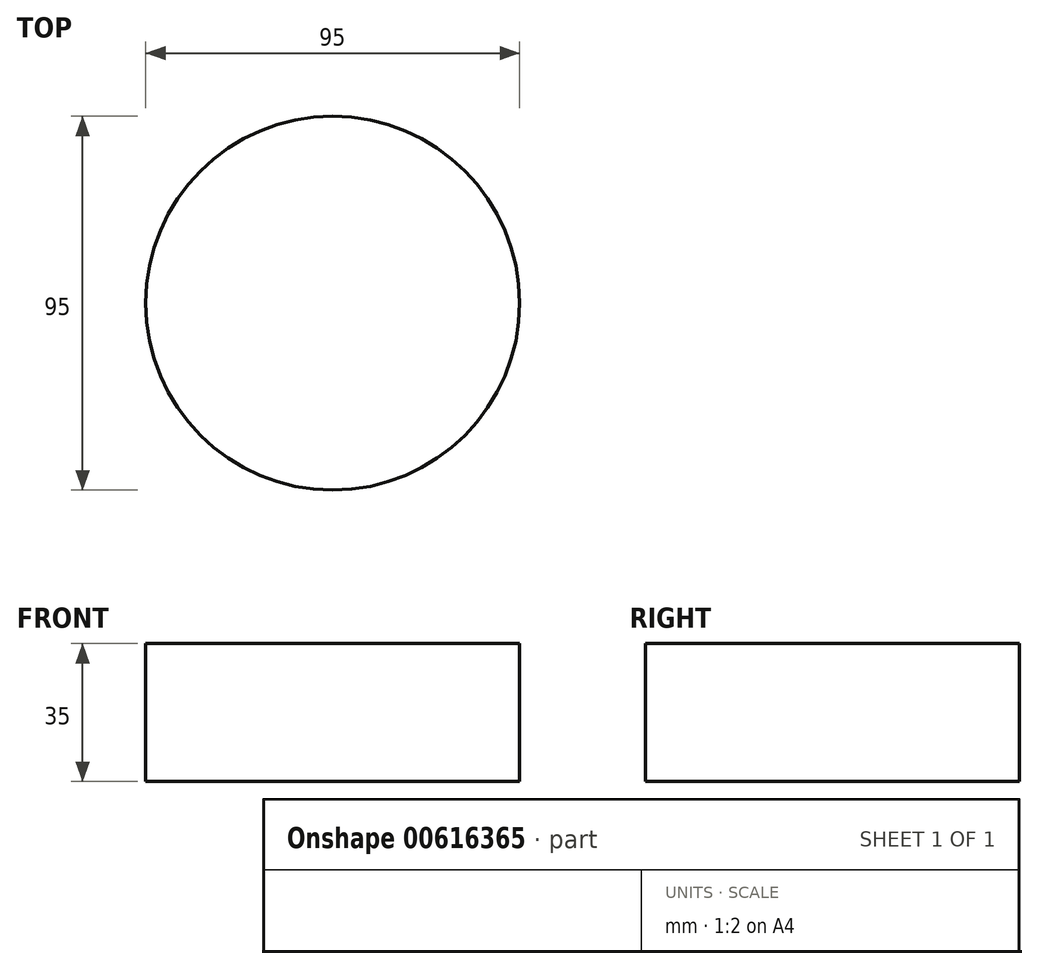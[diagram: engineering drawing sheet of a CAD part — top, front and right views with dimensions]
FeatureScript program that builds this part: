
annotation { "Feature Type Name" : "Feature", "Feature Type Description" : "" }
export const myFeature = defineFeature(function(context is Context, id is Id, definition is map)
    precondition{}
    {
        {
            var Q0;
            Q0=qCreatedBy(makeId("Top.planeOp"),FACE);
            var sketch = newSketch(context, id + "F0", { "sketchPlane" : qUnion([Q0])});
            skCircle(sketch, "E0", {"center": v(0, 0) * mm, "radius": 47.5 * mm});
            skSolve(sketch);
        }
        {
            var Q0;
            Q0 = qSketchRegion(id + "F0", true);
            extrude(context, id + "F1", {"entities" : qUnion([Q0]), "depth" : 35 * mm, "offsetDistance" : 25 * mm});
        }
    });
